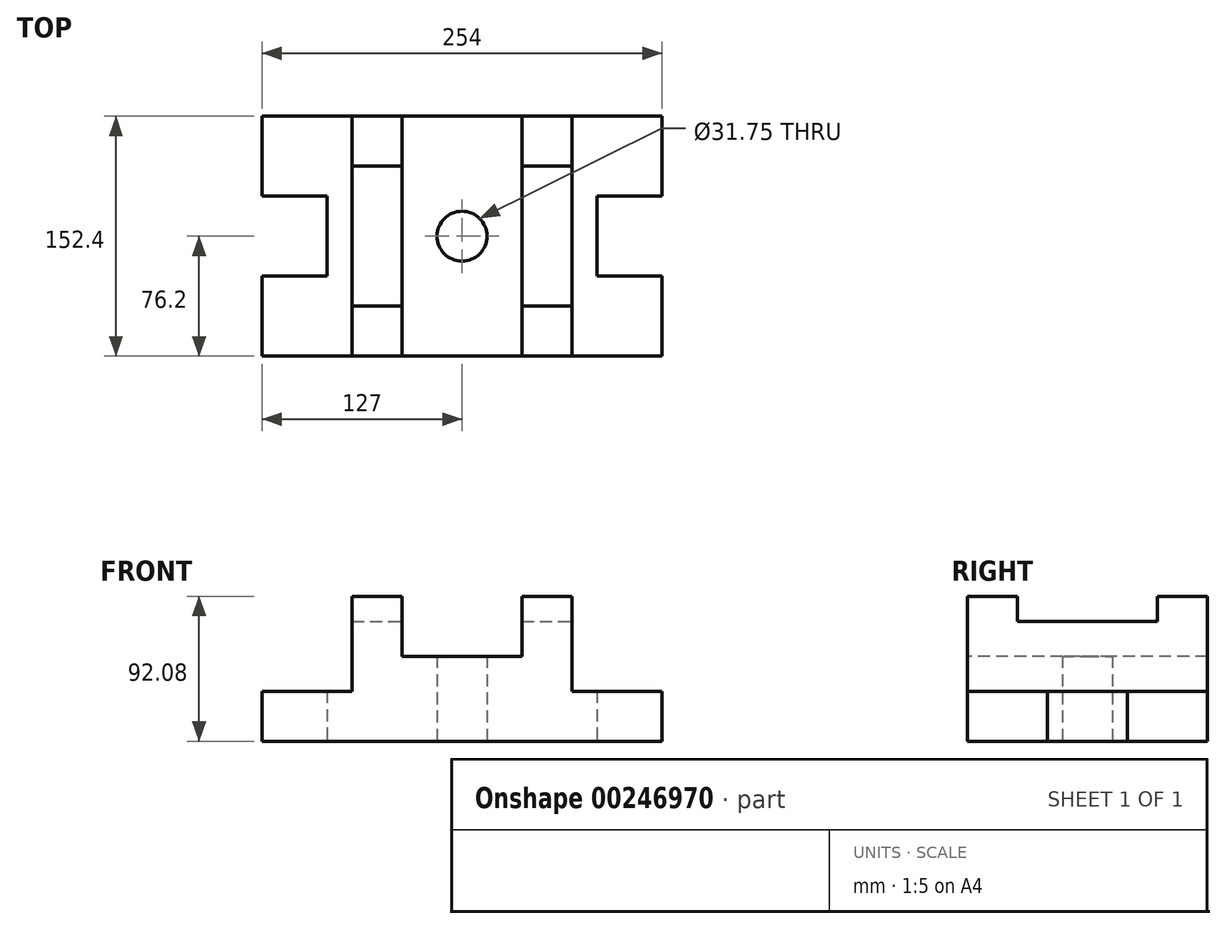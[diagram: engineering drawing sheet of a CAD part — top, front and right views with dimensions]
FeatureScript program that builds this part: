
annotation { "Feature Type Name" : "Feature", "Feature Type Description" : "" }
export const myFeature = defineFeature(function(context is Context, id is Id, definition is map)
    precondition{}
    {
        {
            var Q0;
            Q0=qCreatedBy(makeId("Top.planeOp"),FACE);
            var sketch = newSketch(context, id + "F0", { "sketchPlane" : qUnion([Q0])});
            skCircle(sketch, "E0", {"center": v(0, 0) * mm, "radius": 15.88 * mm});
            skLineSegment(sketch, "E1", {"start": v(127, 76.2) * mm, "end": v(127, -76.2) * mm});
            skLineSegment(sketch, "E2", {"start": v(127, -76.2) * mm, "end": v(-127, -76.2) * mm});
            skLineSegment(sketch, "E3", {"start": v(-127, -76.2) * mm, "end": v(-127, 76.2) * mm});
            skLineSegment(sketch, "E4", {"start": v(-127, 76.2) * mm, "end": v(127, 76.2) * mm});
            skLineSegment(sketch, "E5", {"start": v(127, 25.4) * mm, "end": v(85.72, 25.4) * mm});
            skLineSegment(sketch, "E6", {"start": v(85.72, 25.4) * mm, "end": v(85.72, -25.4) * mm});
            skLineSegment(sketch, "E7", {"start": v(85.72, -25.4) * mm, "end": v(127, -25.4) * mm});
            skLineSegment(sketch, "E8", {"start": v(-127, 25.4) * mm, "end": v(-85.72, 25.4) * mm});
            skLineSegment(sketch, "E9", {"start": v(-85.72, 25.4) * mm, "end": v(-85.72, -25.4) * mm});
            skLineSegment(sketch, "E10", {"start": v(-85.72, -25.4) * mm, "end": v(-127, -25.4) * mm});
            skLineSegment(sketch, "E11", {"start": v(38.1, 76.2) * mm, "end": v(38.1, -76.2) * mm});
            skLineSegment(sketch, "E12", {"start": v(69.85, 76.2) * mm, "end": v(69.85, -76.2) * mm});
            skLineSegment(sketch, "E13", {"start": v(-69.85, 76.2) * mm, "end": v(-69.85, -76.2) * mm});
            skLineSegment(sketch, "E14", {"start": v(-38.1, 76.2) * mm, "end": v(-38.1, -76.2) * mm});
            skLineSegment(sketch, "E15", {"start": v(-69.85, 44.45) * mm, "end": v(-38.1, 44.45) * mm});
            skLineSegment(sketch, "E16", {"start": v(38.1, 44.45) * mm, "end": v(69.85, 44.45) * mm});
            skLineSegment(sketch, "E17", {"start": v(-69.85, -44.45) * mm, "end": v(-38.1, -44.45) * mm});
            skLineSegment(sketch, "E18", {"start": v(38.1, -44.45) * mm, "end": v(69.85, -44.45) * mm});
            skSolve(sketch);
        }
        {
            var Q0;
            {var subQ5=sQuery(id+"F0.wireOp",EDGE,"E18");Q0=makeQuery(id+"F0.imprint","IMPRINT",FACE,{"disambiguationData":[TD([[makeQuery(id+"F0.imprint","IMPRINT",EDGE,{"derivedFrom":subQ5}),-1.0]])]});}
            var Q1;
            {var subQ5=sQuery(id+"F0.wireOp",EDGE,"E17");Q1=makeQuery(id+"F0.imprint","IMPRINT",FACE,{"disambiguationData":[TD([[makeQuery(id+"F0.imprint","IMPRINT",EDGE,{"derivedFrom":subQ5}),-1.0]])]});}
            var Q2;
            {var subQ5=sQuery(id+"F0.wireOp",EDGE,"E15");Q2=makeQuery(id+"F0.imprint","IMPRINT",FACE,{"disambiguationData":[TD([[makeQuery(id+"F0.imprint","IMPRINT",EDGE,{"derivedFrom":subQ5}),1.0]])]});}
            var Q3;
            {var subQ5=sQuery(id+"F0.wireOp",EDGE,"E16");Q3=makeQuery(id+"F0.imprint","IMPRINT",FACE,{"disambiguationData":[TD([[makeQuery(id+"F0.imprint","IMPRINT",EDGE,{"derivedFrom":subQ5}),1.0]])]});}
            var Q4;
            {var subQ9=sQuery(id+"F0.wireOp",EDGE,"E5");Q4=makeQuery(id+"F0.imprint","IMPRINT",FACE,{"disambiguationData":[TD([[makeQuery(id+"F0.imprint","IMPRINT",EDGE,{"derivedFrom":subQ9}),-1.0]])]});}
            var Q5;
            {var subQ5=sQuery(id+"F0.wireOp",EDGE,"E8");Q5=makeQuery(id+"F0.imprint","IMPRINT",FACE,{"disambiguationData":[TD([[makeQuery(id+"F0.imprint","IMPRINT",EDGE,{"derivedFrom":subQ5}),1.0]])]});}
            var Q6;
            Q6=makeQuery(id+"F0.imprint","IMPRINT",FACE,{"disambiguationData":[TD([[makeQuery(id+"F0.imprint","IMPRINT",EDGE,{"derivedFrom":sQuery(id+"F0.wireOp",EDGE,"E0")}),-1.0]])]});
            var Q7;
            {var subQ0=sQuery(id+"F0.wireOp",EDGE,"E16");Q7=makeQuery(id+"F0.imprint","IMPRINT",FACE,{"disambiguationData":[TD([[makeQuery(id+"F0.imprint","IMPRINT",EDGE,{"derivedFrom":subQ0}),-1.0]])]});}
            var Q8;
            {var subQ0=sQuery(id+"F0.wireOp",EDGE,"E15");Q8=makeQuery(id+"F0.imprint","IMPRINT",FACE,{"disambiguationData":[TD([[makeQuery(id+"F0.imprint","IMPRINT",EDGE,{"derivedFrom":subQ0}),-1.0]])]});}
            extrude(context, id + "F1", {"entities" : qUnion([Q0, Q1, Q2, Q3, Q4, Q5, Q6, Q7, Q8]), "depth" : 31.75 * mm});
        }
        {
            var Q0;
            {var subQ5=sQuery(id+"F0.wireOp",EDGE,"E15");Q0=makeQuery(id+"F0.imprint","IMPRINT",FACE,{"disambiguationData":[TD([[makeQuery(id+"F0.imprint","IMPRINT",EDGE,{"derivedFrom":subQ5}),1.0]])]});}
            var Q1;
            {var subQ5=sQuery(id+"F0.wireOp",EDGE,"E17");Q1=makeQuery(id+"F0.imprint","IMPRINT",FACE,{"disambiguationData":[TD([[makeQuery(id+"F0.imprint","IMPRINT",EDGE,{"derivedFrom":subQ5}),-1.0]])]});}
            var Q2;
            {var subQ5=sQuery(id+"F0.wireOp",EDGE,"E16");Q2=makeQuery(id+"F0.imprint","IMPRINT",FACE,{"disambiguationData":[TD([[makeQuery(id+"F0.imprint","IMPRINT",EDGE,{"derivedFrom":subQ5}),1.0]])]});}
            var Q3;
            {var subQ5=sQuery(id+"F0.wireOp",EDGE,"E18");Q3=makeQuery(id+"F0.imprint","IMPRINT",FACE,{"disambiguationData":[TD([[makeQuery(id+"F0.imprint","IMPRINT",EDGE,{"derivedFrom":subQ5}),-1.0]])]});}
            extrude(context, id + "F2", {"entities" : qUnion([Q0, Q1, Q2, Q3]), "operationType" : NewBodyOperationType.ADD, "depth" : 92.07 * mm});
        }
        {
            var Q0;
            {var subQ0=sQuery(id+"F0.wireOp",EDGE,"E15");Q0=makeQuery(id+"F0.imprint","IMPRINT",FACE,{"disambiguationData":[TD([[makeQuery(id+"F0.imprint","IMPRINT",EDGE,{"derivedFrom":subQ0}),-1.0]])]});}
            var Q1;
            {var subQ0=sQuery(id+"F0.wireOp",EDGE,"E16");Q1=makeQuery(id+"F0.imprint","IMPRINT",FACE,{"disambiguationData":[TD([[makeQuery(id+"F0.imprint","IMPRINT",EDGE,{"derivedFrom":subQ0}),-1.0]])]});}
            extrude(context, id + "F3", {"entities" : qUnion([Q0, Q1]), "operationType" : NewBodyOperationType.ADD, "depth" : 76.2 * mm});
        }
        {
            var Q0;
            Q0=makeQuery(id+"F0.imprint","IMPRINT",FACE,{"disambiguationData":[TD([[makeQuery(id+"F0.imprint","IMPRINT",EDGE,{"derivedFrom":sQuery(id+"F0.wireOp",EDGE,"E0")}),-1.0]])]});
            extrude(context, id + "F4", {"entities" : qUnion([Q0]), "operationType" : NewBodyOperationType.ADD, "depth" : 53.97 * mm});
        }
    });
